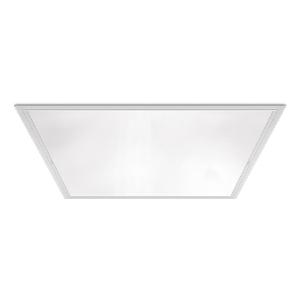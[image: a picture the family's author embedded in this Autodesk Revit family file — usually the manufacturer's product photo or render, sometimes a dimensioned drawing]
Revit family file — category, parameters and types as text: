
# Revit family: 3f_filippi_-_l_340_luce_diffusa_lgs_3f_filippi_-_23859_-_l_340_45w-840_lgs_596x596
name_source: partatom
category: Lighting Fixtures
units: mm (PartAtom-declared; Revit-internal decimal feet)

## family parameters
Cut with Voids When Loaded = No
Host = Face
Light Source = No
Part Type = Normal
Room Calculation Point = No
Round Connector Dimension = Use Diameter
Shared = No

## types (1)
- 3F Filippi - L 340 Luce Diffusa LGS (1 x LED, 6537 lm, 52 W, 4000 K)
    Apparent Load = 52 VA
    Approval mark = ENEC
    CIE Flux Codes = 67 92 98 100 100
    Color Rendering = 80
    Color Temperature = 4000 K
    Control Gear = Electronic ballast
    Default Elevation = 1800 mm
    Description = ILLUMINOTECHNICAL
Luminous efficiency 100% (DLOR 100%, ULOR 0%).
Initial luminous flux of the luminaire 6537 lm.
Direct symmetric distribution.
Installation Interdistance Transv.D = 1.19 x hu - Long.D = 1.17 x hu.
Average luminance <3000 cd/m² for radial angles >65°.
Tabular UGR (CIE 117 - 4H-8H; S=0.25H; 70/50/20): RUG 18.3 - 18.3.
Beam angle: 87° - 86°.
Luminous efficacy 126 lm/W.
Lifetime (L93/B10): 30000 h. (tq+25°C)
Lifetime (L90/B10): 50000 h. (tq+25°C)
Lifetime (L85/B10): 80000 h. (tq+25°C)
Lifetime (L80/B10): 100000 h. (tq+25°C)
Sudden decreased luminous flux after 50000 hours: 0% (C0).
Photobiological safety in compliance with IEC/TR 62778: RG0 risk exempt, (IEC 62471).
In compliance with IEC/EN 62722-2-1 - IEC/EN 62717 standards.

SOURCE
Squared LED module 45W/840.
Energy efficiency class (UE 2019/2020 - UE 2019/2015): C.
CIE 13.3 Colour rendering index: CRI >80 (R9 <50%).
IES TM-30 Fidelity Index: Rf = 84 Rg = 95.
CCT nominal colour temperature 4000 K.
Colour initial tolerance (MacAdam): SDCM 3.

MECHANICAL
Housing in hot-galvanised steel, painted in white polyester.
Perimetral frame in white polycarbonate.
LGS micro-prismatic flat diffuser in transparent methacrylate (PMMA), multi-lenticular exterior, anti-glare.
Anti-glare opal polycarbonate filter for brightness uniformity.
Luminaire with limited surface temperature. - D - (EN 60598-2-24)
Dimensions: 596x596 mm, height 80 mm. Weight 4.4 kg.
IP40 protection degree.
Mechanical strength to impacts IK06 (1 joule).
Glow-wire test resistance 650°C.

ELECTRICAL
Wiring on a separate unit.
Halogen Free electronic wiring 230V-50/60Hz, power factor 0.95, THD <25%, constant output current, SELV, class II, 1 driver.
Power of the luminaire 52 W.
CE - IEC 60598-1 - EN 60598-1.
SAFE FLICKER: PstLM=<1 and SVM=<0.4 (IEC TR 61547-1 and IEC TR 63158), to ensure a more comfortable and safe light.
Luminaire compliant with EN 60598-2-22 for power supply from a centralised emergency system CPSS (Central Power Supply System), not incorporated in the luminaire - high risk areas excluded. The default power and flux are 100% in AC and 100% in DC.
Ambient temperature from 0°C to +40°C.
Temperature class T6 max 85°C.
Relative humidity UR: <85%.

INSTALLATION
Lay-on or pull-up recessed fitting using frame accessory.
All accessories dedicated to this product are available on the Catalog and on our website www.3F-Filippi.com.

APPLICATIONS
Suitable product for food production plants (HACCP), IFS (Food Version 6), BRC (GSFS Food Version 7).
Environments: with VDTs, meeting rooms, offices.
Environments: architectural, commercial, staterooms, banks.
Environments where demanding visual tasks are performed and soft diffuse light is required for optimal visual comfort and total shielding of the light source.

WARNING
Luminaire designed for disposal/recycling at end-of-life.
Replaceable (LED only) light source by a professional. Replaceable control gear by a professional.
    Height = 0 mm  [stored 0 ft]
    Lamp = 1 x LED
    Lamp Light Flux = 6537 lm
    Lamp Power = 52 W
    Lamp count = 1
    Length = 596 mm
    Lifetime = 50000 h
    Luminous efficacy = 126 lm/W
    Manufacturer = 3F Filippi
    ModVariant = No
    Model = 3F Filippi - 23859 - L 340 45W-840 LGS 596x596
    Mounting Place = Ceiling
    Mounting Type = Recessed
    Number of Poles = 1
    OnlyDefault = Yes
    Power Factor = 1
    Product Name = 3F Filippi - L 340 Luce Diffusa LGS
    Product group = recessed luminaire
    ProductGroupID = 4
    Protection Class = Protection class II
    Protection Degree = IP 40
    RLX_Detail_Level = 1
    RLX_Emergency_Light_Flux = 0 lm
    RLX_Emergency_Type = 0
    RLX_Emergency_Type_DB = No
    RlxData = <blob elided: 153053 chars, md5=b3dfaa02>
    Socket = socket
    Standby Power = 0 W
    System Light Flux = 6537 lm
    System Power = 52 W
    Type Comments = Product without accessories
    Type Image = 3ffilippi_l_340_luce_diffusa_lgs.jpg
    URL = http://relux.com
    VarID = ---
    Voltage = 0 V
    Weight = 0.00 kg
    Width = 596 mm

note: [stored X ft] marks values corroborated as IEEE doubles in the binary element streams (Revit-internal decimal feet)

## geometry (parser evidence)
native form markers: Blend x4, Sweep x10
no freeform markers — native parametric forms only
